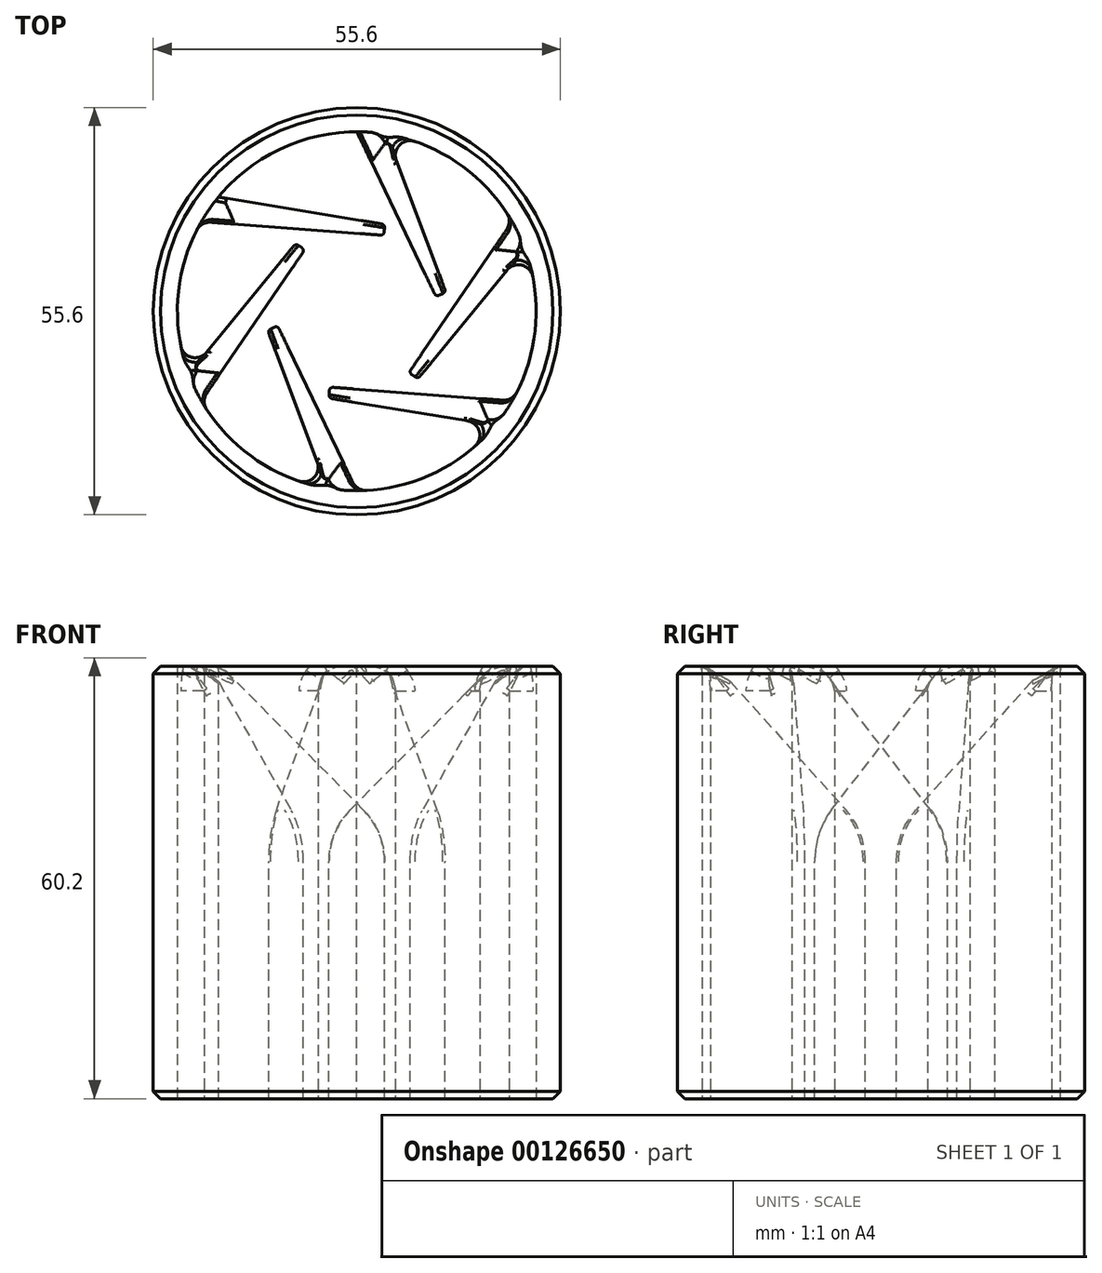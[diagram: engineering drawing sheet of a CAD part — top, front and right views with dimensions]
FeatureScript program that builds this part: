
annotation { "Feature Type Name" : "Feature", "Feature Type Description" : "" }
export const myFeature = defineFeature(function(context is Context, id is Id, definition is map)
    precondition{}
    {
        {
            var Q0;
            Q0=qCreatedBy(makeId("Top.planeOp"),FACE);
            var sketch = newSketch(context, id + "F0", { "sketchPlane" : qUnion([Q0])});
            skCircle(sketch, "E0", {"center": v(0, 0) * mm, "radius": 27.8 * mm});
            skCircle(sketch, "E1", {"center": v(0, 0) * mm, "radius": 24.5 * mm});
            skSolve(sketch);
        }
        {
            var Q0;
            Q0 = qSketchRegion(id + "F0", true);
            extrude(context, id + "F1", {"entities" : qUnion([Q0]), "depth" : 59 * mm});
        }
        {
            var Q0;
            Q0=makeQuery(id+"F1.opExtrude","CAP_FACE",FACE,{"disambiguationData":[OSD([sQuery(id+"F0.wireOp",EDGE,"E0"),sQuery(id+"F0.wireOp",EDGE,"E1")])],"isStart":false});
            var sketch = newSketch(context, id + "F2", { "sketchPlane" : qUnion([Q0])});
            skArc(sketch, "E2.0", {"start": v(4.05, 24.16) * mm, "mid": v(2.03, 24.42) * mm, "end": v(0, 24.5) * mm});
            skLineSegment(sketch, "E3", {"start": v(0, 24.5) * mm, "end": v(10.82, 1.96) * mm});
            skLineSegment(sketch, "E4", {"start": v(10.82, 1.96) * mm, "end": v(12.18, 2.61) * mm});
            skLineSegment(sketch, "E5", {"start": v(12.18, 2.61) * mm, "end": v(4.05, 24.16) * mm});
            skArc(sketch, "E6.1.0", {"start": v(-18.9, 15.6) * mm, "mid": v(-20.13, 13.97) * mm, "end": v(-21.22, 12.25) * mm});
            skLineSegment(sketch, "E6.1.1", {"start": v(-21.22, 12.25) * mm, "end": v(3.71, 10.36) * mm});
            skLineSegment(sketch, "E6.1.2", {"start": v(3.71, 10.36) * mm, "end": v(3.82, 11.85) * mm});
            skLineSegment(sketch, "E6.1.3", {"start": v(3.82, 11.85) * mm, "end": v(-18.9, 15.6) * mm});
            skArc(sketch, "E6.2.0", {"start": v(-22.95, -8.57) * mm, "mid": v(-22.16, -10.45) * mm, "end": v(-21.22, -12.25) * mm});
            skLineSegment(sketch, "E6.2.1", {"start": v(-21.22, -12.25) * mm, "end": v(-7.11, 8.4) * mm});
            skLineSegment(sketch, "E6.2.2", {"start": v(-7.11, 8.4) * mm, "end": v(-8.35, 9.24) * mm});
            skLineSegment(sketch, "E6.2.3", {"start": v(-8.35, 9.24) * mm, "end": v(-22.95, -8.57) * mm});
            skArc(sketch, "E7.1.3.0", {"start": v(-4.05, -24.16) * mm, "mid": v(-2.03, -24.42) * mm, "end": v(0, -24.5) * mm});
            skLineSegment(sketch, "E7.4.3.0", {"start": v(0, -24.5) * mm, "end": v(-10.82, -1.96) * mm});
            skLineSegment(sketch, "E7.7.3.0", {"start": v(-10.82, -1.96) * mm, "end": v(-12.18, -2.61) * mm});
            skLineSegment(sketch, "E7.10.3.0", {"start": v(-12.18, -2.61) * mm, "end": v(-4.05, -24.16) * mm});
            skArc(sketch, "E7.1.4.0", {"start": v(18.9, -15.6) * mm, "mid": v(20.13, -13.97) * mm, "end": v(21.22, -12.25) * mm});
            skLineSegment(sketch, "E7.4.4.0", {"start": v(21.22, -12.25) * mm, "end": v(-3.71, -10.36) * mm});
            skLineSegment(sketch, "E7.7.4.0", {"start": v(-3.71, -10.36) * mm, "end": v(-3.82, -11.85) * mm});
            skLineSegment(sketch, "E7.10.4.0", {"start": v(-3.82, -11.85) * mm, "end": v(18.9, -15.6) * mm});
            skArc(sketch, "E7.1.5.0", {"start": v(22.95, 8.57) * mm, "mid": v(22.16, 10.45) * mm, "end": v(21.22, 12.25) * mm});
            skLineSegment(sketch, "E7.4.5.0", {"start": v(21.22, 12.25) * mm, "end": v(7.11, -8.4) * mm});
            skLineSegment(sketch, "E7.7.5.0", {"start": v(7.11, -8.4) * mm, "end": v(8.35, -9.24) * mm});
            skLineSegment(sketch, "E7.10.5.0", {"start": v(8.35, -9.24) * mm, "end": v(22.95, 8.57) * mm});
            skCircle(sketch, "E8", {"center": v(0, 0) * mm, "radius": 11 * mm, "construction": true});
            skLineSegment(sketch, "E9", {"start": v(4.05, 24.16) * mm, "end": v(0.76, 22.92) * mm, "construction": true});
            skSolve(sketch);
        }
        {
            var Q0;
            Q0=makeQuery(id+"F2.imprint","IMPRINT",FACE,{"disambiguationData":[TD([[makeQuery(id+"F2.imprint","IMPRINT",EDGE,{"derivedFrom":sQuery(id+"F2.wireOp",EDGE,"E6.1.0")}),1.0]])]});
            var Q1;
            Q1=makeQuery(id+"F2.imprint","IMPRINT",FACE,{"disambiguationData":[TD([[makeQuery(id+"F2.imprint","IMPRINT",EDGE,{"derivedFrom":sQuery(id+"F2.wireOp",EDGE,"E2.0")}),1.0]])]});
            var Q2;
            Q2=makeQuery(id+"F2.imprint","IMPRINT",FACE,{"disambiguationData":[TD([[makeQuery(id+"F2.imprint","IMPRINT",EDGE,{"derivedFrom":sQuery(id+"F2.wireOp",EDGE,"E7.1.5.0")}),1.0]])]});
            var Q3;
            Q3=makeQuery(id+"F2.imprint","IMPRINT",FACE,{"disambiguationData":[TD([[makeQuery(id+"F2.imprint","IMPRINT",EDGE,{"derivedFrom":sQuery(id+"F2.wireOp",EDGE,"E7.1.4.0")}),1.0]])]});
            var Q4;
            Q4=makeQuery(id+"F2.imprint","IMPRINT",FACE,{"disambiguationData":[TD([[makeQuery(id+"F2.imprint","IMPRINT",EDGE,{"derivedFrom":sQuery(id+"F2.wireOp",EDGE,"E7.1.3.0")}),1.0]])]});
            var Q5;
            Q5=makeQuery(id+"F2.imprint","IMPRINT",FACE,{"disambiguationData":[TD([[makeQuery(id+"F2.imprint","IMPRINT",EDGE,{"derivedFrom":sQuery(id+"F2.wireOp",EDGE,"E6.2.0")}),1.0]])]});
            var Q6;
            Q6=makeQuery(id+"F1.opExtrude","CAP_FACE",FACE,{"disambiguationData":[OSD([sQuery(id+"F0.wireOp",EDGE,"E0"),sQuery(id+"F0.wireOp",EDGE,"E1")])],"isStart":true});
            extrude(context, id + "F3", {"entities" : qUnion([Q0, Q1, Q2, Q3, Q4, Q5]), "operationType" : NewBodyOperationType.ADD, "endBound" : BoundingType.UP_TO_SURFACE, "oppositeDirection" : true, "endBoundEntityFace" : qUnion([Q6]), "depth" : 25 * mm});
        }
        {
            var Q0;
            Q0=makeQuery(id+"F3.opExtrude","CAP_EDGE",EDGE,{"disambiguationData":[OSD([sQuery(id+"F2.wireOp",EDGE,"E4")])],"isStart":true});
            var Q1;
            Q1=makeQuery(id+"F3.opExtrude","CAP_EDGE",EDGE,{"disambiguationData":[OSD([sQuery(id+"F2.wireOp",EDGE,"E7.7.5.0")])],"isStart":true});
            var Q2;
            Q2=makeQuery(id+"F3.opExtrude","CAP_EDGE",EDGE,{"disambiguationData":[OSD([sQuery(id+"F2.wireOp",EDGE,"E7.7.4.0")])],"isStart":true});
            var Q3;
            Q3=makeQuery(id+"F3.opExtrude","CAP_EDGE",EDGE,{"disambiguationData":[OSD([sQuery(id+"F2.wireOp",EDGE,"E7.7.3.0")])],"isStart":true});
            var Q4;
            Q4=makeQuery(id+"F3.opExtrude","CAP_EDGE",EDGE,{"disambiguationData":[OSD([sQuery(id+"F2.wireOp",EDGE,"E6.2.2")])],"isStart":true});
            var Q5;
            Q5=makeQuery(id+"F3.opExtrude","CAP_EDGE",EDGE,{"disambiguationData":[OSD([sQuery(id+"F2.wireOp",EDGE,"E6.1.2")])],"isStart":true});
            chamfer(context, id + "F4", {"entities" : qUnion([Q0, Q1, Q2, Q3, Q4, Q5]), "width" : 22.5 * mm, "tangentPropagation" : true});
        }
        {
            var Q0;
            Q0=qCreatedBy(makeId("Right.planeOp"),FACE);
            var sketch = newSketch(context, id + "F5", { "sketchPlane" : qUnion([Q0])});
            skLineSegment(sketch, "E10", {"start": v(24.5, 59) * mm, "end": v(0, 46.02) * mm});
            skLineSegment(sketch, "E11", {"start": v(0, 59) * mm, "end": v(0, 46.02) * mm});
            skLineSegment(sketch, "E12", {"start": v(0, 59) * mm, "end": v(24.5, 59) * mm});
            skSolve(sketch);
        }
        {
            var Q0;
            Q0 = qSketchRegion(id + "F5", true);
            var Q1;
            Q1=sQuery(id+"F5.wireOp",EDGE,"E11");
            revolve(context, id + "F6", {"operationType" : NewBodyOperationType.REMOVE, "entities" : qUnion([Q0]), "axis" : qUnion([Q1]), "revolveType" : RevolveType.FULL});
        }
        {
            var Q0;
            Q0=makeQuery(id+"F6.boolean.opBoolean","INTERSECT",EDGE,{"derivedFrom":[makeQuery(id+"F3.opExtrude","SWEPT_FACE",FACE,{"disambiguationData":[OSD([sQuery(id+"F2.wireOp",EDGE,"E7.10.3.0")])]}),makeQuery(id+"F6.opRevolve","SWEPT_FACE",FACE,{"disambiguationData":[OSD([sQuery(id+"F5.wireOp",EDGE,"E10")])]})]});
            var Q1;
            Q1=makeQuery(id+"F6.boolean.opBoolean","INTERSECT",EDGE,{"derivedFrom":[makeQuery(id+"F3.opExtrude","SWEPT_FACE",FACE,{"disambiguationData":[OSD([sQuery(id+"F2.wireOp",EDGE,"E7.4.3.0")])]}),makeQuery(id+"F6.opRevolve","SWEPT_FACE",FACE,{"disambiguationData":[OSD([sQuery(id+"F5.wireOp",EDGE,"E10")])]})]});
            var Q2;
            Q2=makeQuery(id+"F6.boolean.opBoolean","INTERSECT",EDGE,{"derivedFrom":[makeQuery(id+"F3.opExtrude","SWEPT_FACE",FACE,{"disambiguationData":[OSD([sQuery(id+"F2.wireOp",EDGE,"E6.2.1")])]}),makeQuery(id+"F6.opRevolve","SWEPT_FACE",FACE,{"disambiguationData":[OSD([sQuery(id+"F5.wireOp",EDGE,"E10")])]})]});
            var Q3;
            Q3=makeQuery(id+"F6.boolean.opBoolean","INTERSECT",EDGE,{"derivedFrom":[makeQuery(id+"F3.opExtrude","SWEPT_FACE",FACE,{"disambiguationData":[OSD([sQuery(id+"F2.wireOp",EDGE,"E6.2.3")])]}),makeQuery(id+"F6.opRevolve","SWEPT_FACE",FACE,{"disambiguationData":[OSD([sQuery(id+"F5.wireOp",EDGE,"E10")])]})]});
            var Q4;
            Q4=makeQuery(id+"F6.boolean.opBoolean","INTERSECT",EDGE,{"derivedFrom":[makeQuery(id+"F3.opExtrude","SWEPT_FACE",FACE,{"disambiguationData":[OSD([sQuery(id+"F2.wireOp",EDGE,"E6.1.1")])]}),makeQuery(id+"F6.opRevolve","SWEPT_FACE",FACE,{"disambiguationData":[OSD([sQuery(id+"F5.wireOp",EDGE,"E10")])]})]});
            var Q5;
            Q5=makeQuery(id+"F6.boolean.opBoolean","INTERSECT",EDGE,{"derivedFrom":[makeQuery(id+"F3.opExtrude","SWEPT_FACE",FACE,{"disambiguationData":[OSD([sQuery(id+"F2.wireOp",EDGE,"E6.1.3")])]}),makeQuery(id+"F6.opRevolve","SWEPT_FACE",FACE,{"disambiguationData":[OSD([sQuery(id+"F5.wireOp",EDGE,"E10")])]})]});
            var Q6;
            Q6=makeQuery(id+"F6.boolean.opBoolean","INTERSECT",EDGE,{"derivedFrom":[makeQuery(id+"F3.opExtrude","SWEPT_FACE",FACE,{"disambiguationData":[OSD([sQuery(id+"F2.wireOp",EDGE,"E3")])]}),makeQuery(id+"F6.opRevolve","SWEPT_FACE",FACE,{"disambiguationData":[OSD([sQuery(id+"F5.wireOp",EDGE,"E10")])]})]});
            var Q7;
            Q7=makeQuery(id+"F6.boolean.opBoolean","INTERSECT",EDGE,{"derivedFrom":[makeQuery(id+"F3.opExtrude","SWEPT_FACE",FACE,{"disambiguationData":[OSD([sQuery(id+"F2.wireOp",EDGE,"E5")])]}),makeQuery(id+"F6.opRevolve","SWEPT_FACE",FACE,{"disambiguationData":[OSD([sQuery(id+"F5.wireOp",EDGE,"E10")])]})]});
            var Q8;
            Q8=makeQuery(id+"F6.boolean.opBoolean","INTERSECT",EDGE,{"derivedFrom":[makeQuery(id+"F3.opExtrude","SWEPT_FACE",FACE,{"disambiguationData":[OSD([sQuery(id+"F2.wireOp",EDGE,"E7.4.5.0")])]}),makeQuery(id+"F6.opRevolve","SWEPT_FACE",FACE,{"disambiguationData":[OSD([sQuery(id+"F5.wireOp",EDGE,"E10")])]})]});
            var Q9;
            Q9=makeQuery(id+"F6.boolean.opBoolean","INTERSECT",EDGE,{"derivedFrom":[makeQuery(id+"F3.opExtrude","SWEPT_FACE",FACE,{"disambiguationData":[OSD([sQuery(id+"F2.wireOp",EDGE,"E7.10.5.0")])]}),makeQuery(id+"F6.opRevolve","SWEPT_FACE",FACE,{"disambiguationData":[OSD([sQuery(id+"F5.wireOp",EDGE,"E10")])]})]});
            var Q10;
            Q10=makeQuery(id+"F6.boolean.opBoolean","INTERSECT",EDGE,{"derivedFrom":[makeQuery(id+"F3.opExtrude","SWEPT_FACE",FACE,{"disambiguationData":[OSD([sQuery(id+"F2.wireOp",EDGE,"E7.4.4.0")])]}),makeQuery(id+"F6.opRevolve","SWEPT_FACE",FACE,{"disambiguationData":[OSD([sQuery(id+"F5.wireOp",EDGE,"E10")])]})]});
            var Q11;
            Q11=makeQuery(id+"F6.boolean.opBoolean","INTERSECT",EDGE,{"derivedFrom":[makeQuery(id+"F3.opExtrude","SWEPT_FACE",FACE,{"disambiguationData":[OSD([sQuery(id+"F2.wireOp",EDGE,"E7.10.4.0")])]}),makeQuery(id+"F6.opRevolve","SWEPT_FACE",FACE,{"disambiguationData":[OSD([sQuery(id+"F5.wireOp",EDGE,"E10")])]})]});
            fillet(context, id + "F7", {"entities" : qUnion([Q0, Q1, Q2, Q3, Q4, Q5, Q6, Q7, Q8, Q9, Q10, Q11]), "radius" : 0.5 * mm, "tangentPropagation" : true, "allowEdgeOverflow" : false});
        }
        {
            var Q0;
            Q0=makeQuery(id+"F3.opExtrude","SWEPT_EDGE",EDGE,{"disambiguationData":[OSD([sQuery(id+"F0.wireOp",EDGE,"E1"),sQuery(id+"F2.wireOp",EDGE,"E7.1.3.0"),sQuery(id+"F2.wireOp",EDGE,"E7.4.3.0")])]});
            var Q1;
            Q1=makeQuery(id+"F3.opExtrude","SWEPT_EDGE",EDGE,{"disambiguationData":[OSD([sQuery(id+"F0.wireOp",EDGE,"E1"),sQuery(id+"F2.wireOp",EDGE,"E6.2.0"),sQuery(id+"F2.wireOp",EDGE,"E6.2.1")])]});
            var Q2;
            Q2=makeQuery(id+"F3.opExtrude","SWEPT_EDGE",EDGE,{"disambiguationData":[OSD([sQuery(id+"F0.wireOp",EDGE,"E1"),sQuery(id+"F2.wireOp",EDGE,"E6.1.0"),sQuery(id+"F2.wireOp",EDGE,"E6.1.3")])]});
            var Q3;
            Q3=makeQuery(id+"F3.opExtrude","SWEPT_EDGE",EDGE,{"disambiguationData":[OSD([sQuery(id+"F0.wireOp",EDGE,"E1"),sQuery(id+"F2.wireOp",EDGE,"E7.1.4.0"),sQuery(id+"F2.wireOp",EDGE,"E7.4.4.0")])]});
            var Q4;
            Q4=makeQuery(id+"F3.opExtrude","SWEPT_EDGE",EDGE,{"disambiguationData":[OSD([sQuery(id+"F0.wireOp",EDGE,"E1"),sQuery(id+"F2.wireOp",EDGE,"E7.1.3.0"),sQuery(id+"F2.wireOp",EDGE,"E7.10.3.0")])]});
            var Q5;
            Q5=makeQuery(id+"F3.opExtrude","SWEPT_EDGE",EDGE,{"disambiguationData":[OSD([sQuery(id+"F0.wireOp",EDGE,"E1"),sQuery(id+"F2.wireOp",EDGE,"E7.1.5.0"),sQuery(id+"F2.wireOp",EDGE,"E7.4.5.0")])]});
            var Q6;
            Q6=makeQuery(id+"F3.opExtrude","SWEPT_EDGE",EDGE,{"disambiguationData":[OSD([sQuery(id+"F0.wireOp",EDGE,"E1"),sQuery(id+"F2.wireOp",EDGE,"E2.0"),sQuery(id+"F2.wireOp",EDGE,"E3")])]});
            var Q7;
            Q7=makeQuery(id+"F3.opExtrude","SWEPT_EDGE",EDGE,{"disambiguationData":[OSD([sQuery(id+"F0.wireOp",EDGE,"E1"),sQuery(id+"F2.wireOp",EDGE,"E7.1.5.0"),sQuery(id+"F2.wireOp",EDGE,"E7.10.5.0")])]});
            var Q8;
            Q8=makeQuery(id+"F3.opExtrude","SWEPT_EDGE",EDGE,{"disambiguationData":[OSD([sQuery(id+"F0.wireOp",EDGE,"E1"),sQuery(id+"F2.wireOp",EDGE,"E6.2.0"),sQuery(id+"F2.wireOp",EDGE,"E6.2.3")])]});
            var Q9;
            Q9=makeQuery(id+"F3.opExtrude","SWEPT_EDGE",EDGE,{"disambiguationData":[OSD([sQuery(id+"F0.wireOp",EDGE,"E1"),sQuery(id+"F2.wireOp",EDGE,"E7.1.4.0"),sQuery(id+"F2.wireOp",EDGE,"E7.10.4.0")])]});
            var Q10;
            Q10=makeQuery(id+"F3.opExtrude","SWEPT_EDGE",EDGE,{"disambiguationData":[OSD([sQuery(id+"F0.wireOp",EDGE,"E1"),sQuery(id+"F2.wireOp",EDGE,"E6.1.0"),sQuery(id+"F2.wireOp",EDGE,"E6.1.1")])]});
            var Q11;
            Q11=makeQuery(id+"F3.opExtrude","SWEPT_EDGE",EDGE,{"disambiguationData":[OSD([sQuery(id+"F0.wireOp",EDGE,"E1"),sQuery(id+"F2.wireOp",EDGE,"E2.0"),sQuery(id+"F2.wireOp",EDGE,"E5")])]});
            fillet(context, id + "F8", {"entities" : qUnion([Q0, Q1, Q2, Q3, Q4, Q5, Q6, Q7, Q8, Q9, Q10, Q11]), "radius" : 2 * mm, "tangentPropagation" : true, "allowEdgeOverflow" : false});
        }
        {
            var Q0;
            Q0=makeQuery(id+"F1.opExtrude","CAP_EDGE",EDGE,{"disambiguationData":[OSD([sQuery(id+"F0.wireOp",EDGE,"E0")])],"isStart":false});
            var Q1;
            Q1=makeQuery(id+"F1.opExtrude","CAP_EDGE",EDGE,{"disambiguationData":[OSD([sQuery(id+"F0.wireOp",EDGE,"E0")])],"isStart":true});
            chamfer(context, id + "F9", {"entities" : qUnion([Q0, Q1]), "width" : 1 * mm, "tangentPropagation" : true});
        }
        {
            var Q0;
            {var subQ0=sQuery(id+"F2.wireOp",EDGE,"E7.7.4.0");Q0=makeQuery(id+"F4.opChamfer","BLEND_EDGE",EDGE,{"blendedFrom":[makeQuery(id+"F3.opExtrude","CAP_EDGE",EDGE,{"disambiguationData":[OSD([subQ0])],"isStart":true}),makeQuery(id+"F3.opExtrude","SWEPT_FACE",FACE,{"disambiguationData":[OSD([subQ0])]})],"blendedInto":[makeQuery(id+"F3.opExtrude","SWEPT_FACE",FACE,{"disambiguationData":[OSD([subQ0])]})]});}
            var Q1;
            {var subQ0=sQuery(id+"F2.wireOp",EDGE,"E7.7.3.0");Q1=makeQuery(id+"F4.opChamfer","BLEND_EDGE",EDGE,{"blendedFrom":[makeQuery(id+"F3.opExtrude","CAP_EDGE",EDGE,{"disambiguationData":[OSD([subQ0])],"isStart":true}),makeQuery(id+"F3.opExtrude","SWEPT_FACE",FACE,{"disambiguationData":[OSD([subQ0])]})],"blendedInto":[makeQuery(id+"F3.opExtrude","SWEPT_FACE",FACE,{"disambiguationData":[OSD([subQ0])]})]});}
            var Q2;
            {var subQ0=sQuery(id+"F2.wireOp",EDGE,"E6.2.2");Q2=makeQuery(id+"F4.opChamfer","BLEND_EDGE",EDGE,{"blendedFrom":[makeQuery(id+"F3.opExtrude","CAP_EDGE",EDGE,{"disambiguationData":[OSD([subQ0])],"isStart":true}),makeQuery(id+"F3.opExtrude","SWEPT_FACE",FACE,{"disambiguationData":[OSD([subQ0])]})],"blendedInto":[makeQuery(id+"F3.opExtrude","SWEPT_FACE",FACE,{"disambiguationData":[OSD([subQ0])]})]});}
            var Q3;
            {var subQ0=sQuery(id+"F2.wireOp",EDGE,"E6.1.2");Q3=makeQuery(id+"F4.opChamfer","BLEND_EDGE",EDGE,{"blendedFrom":[makeQuery(id+"F3.opExtrude","CAP_EDGE",EDGE,{"disambiguationData":[OSD([subQ0])],"isStart":true}),makeQuery(id+"F3.opExtrude","SWEPT_FACE",FACE,{"disambiguationData":[OSD([subQ0])]})],"blendedInto":[makeQuery(id+"F3.opExtrude","SWEPT_FACE",FACE,{"disambiguationData":[OSD([subQ0])]})]});}
            var Q4;
            {var subQ0=sQuery(id+"F2.wireOp",EDGE,"E4");Q4=makeQuery(id+"F4.opChamfer","BLEND_EDGE",EDGE,{"blendedFrom":[makeQuery(id+"F3.opExtrude","CAP_EDGE",EDGE,{"disambiguationData":[OSD([subQ0])],"isStart":true}),makeQuery(id+"F3.opExtrude","SWEPT_FACE",FACE,{"disambiguationData":[OSD([subQ0])]})],"blendedInto":[makeQuery(id+"F3.opExtrude","SWEPT_FACE",FACE,{"disambiguationData":[OSD([subQ0])]})]});}
            var Q5;
            {var subQ0=sQuery(id+"F2.wireOp",EDGE,"E7.7.5.0");Q5=makeQuery(id+"F4.opChamfer","BLEND_EDGE",EDGE,{"blendedFrom":[makeQuery(id+"F3.opExtrude","CAP_EDGE",EDGE,{"disambiguationData":[OSD([subQ0])],"isStart":true}),makeQuery(id+"F3.opExtrude","SWEPT_FACE",FACE,{"disambiguationData":[OSD([subQ0])]})],"blendedInto":[makeQuery(id+"F3.opExtrude","SWEPT_FACE",FACE,{"disambiguationData":[OSD([subQ0])]})]});}
            fillet(context, id + "F10", {"entities" : qUnion([Q0, Q1, Q2, Q3, Q4, Q5]), "radius" : 10 * mm, "tangentPropagation" : true, "allowEdgeOverflow" : false});
        }
        {
            var Q0;
            Q0=makeQuery(id+"F4.opChamfer","BLEND_FACE",FACE,{"disambiguationData":[OSD([sQuery(id+"F2.wireOp",EDGE,"E7.7.3.0")])]});
            var Q1;
            Q1=makeQuery(id+"F4.opChamfer","BLEND_FACE",FACE,{"disambiguationData":[OSD([sQuery(id+"F2.wireOp",EDGE,"E7.7.4.0")])]});
            var Q2;
            Q2=makeQuery(id+"F4.opChamfer","BLEND_FACE",FACE,{"disambiguationData":[OSD([sQuery(id+"F2.wireOp",EDGE,"E7.7.5.0")])]});
            var Q3;
            Q3=makeQuery(id+"F4.opChamfer","BLEND_FACE",FACE,{"disambiguationData":[OSD([sQuery(id+"F2.wireOp",EDGE,"E4")])]});
            var Q4;
            Q4=makeQuery(id+"F4.opChamfer","BLEND_FACE",FACE,{"disambiguationData":[OSD([sQuery(id+"F2.wireOp",EDGE,"E6.2.2")])]});
            var Q5;
            Q5=makeQuery(id+"F4.opChamfer","BLEND_FACE",FACE,{"disambiguationData":[OSD([sQuery(id+"F2.wireOp",EDGE,"E6.1.2")])]});
            fillet(context, id + "F11", {"entities" : qUnion([Q0, Q1, Q2, Q3, Q4, Q5]), "radius" : 0.5 * mm, "tangentPropagation" : true, "allowEdgeOverflow" : false});
        }
    });
